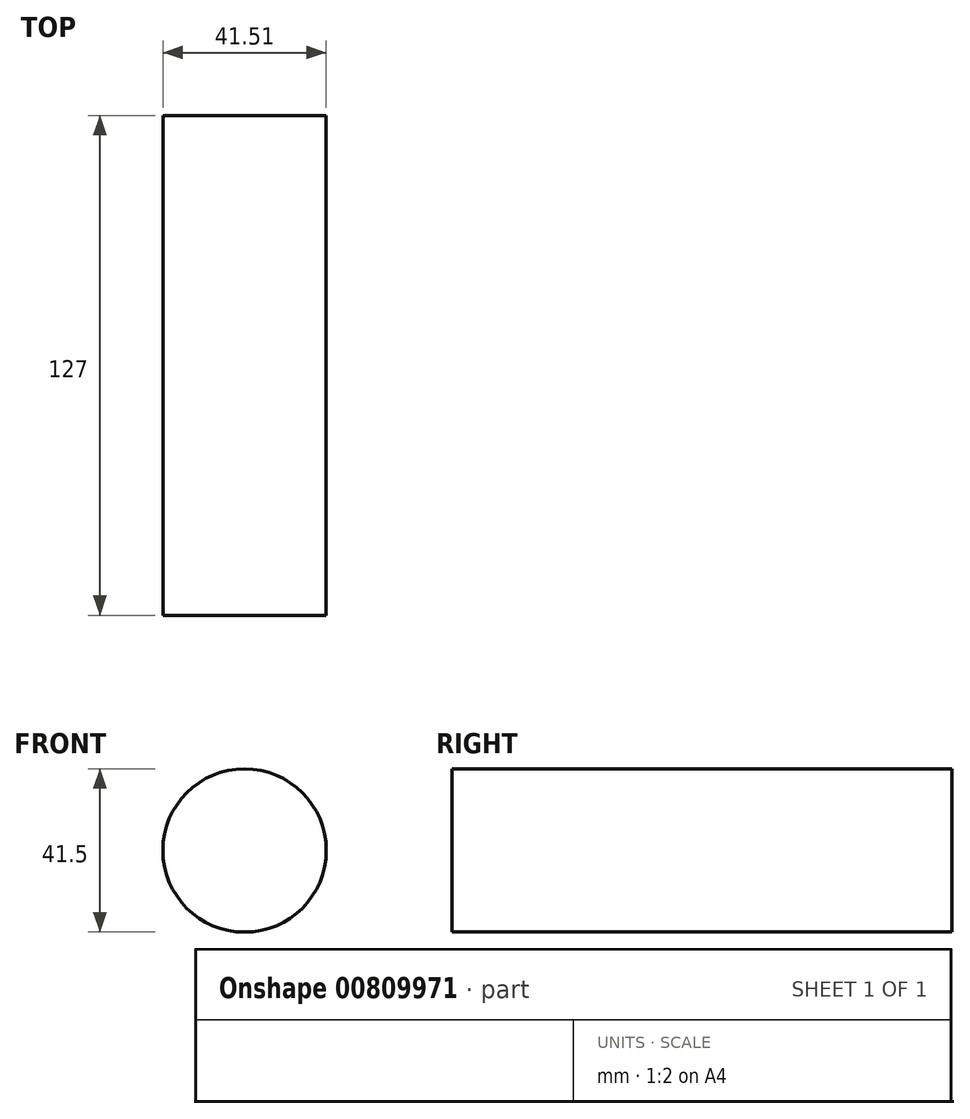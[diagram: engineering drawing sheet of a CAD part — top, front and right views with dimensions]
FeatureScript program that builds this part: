
annotation { "Feature Type Name" : "Feature", "Feature Type Description" : "" }
export const myFeature = defineFeature(function(context is Context, id is Id, definition is map)
    precondition{}
    {
        {
            var Q0;
            Q0=qCreatedBy(makeId("Front.planeOp"),FACE);
            var sketch = newSketch(context, id + "F0", { "sketchPlane" : qUnion([Q0])});
            skCircle(sketch, "E0", {"center": v(0, 0) * mm, "radius": 23.78 * mm});
            skCircle(sketch, "E1", {"center": v(55.11, 0) * mm, "radius": 21.23 * mm});
            skCircle(sketch, "E2", {"center": v(-55.84, 0) * mm, "radius": 20.75 * mm});
            skSolve(sketch);
        }
        {
            var Q0;
            Q0=makeQuery(id+"F0.imprint","IMPRINT",FACE,{"disambiguationData":[TD([[makeQuery(id+"F0.imprint","IMPRINT",EDGE,{"derivedFrom":sQuery(id+"F0.wireOp",EDGE,"E2")}),1.0]])]});
            extrude(context, id + "F1", {"entities" : qUnion([Q0]), "depth" : 127 * mm, "offsetDistance" : 25.4 * mm});
        }
    });
